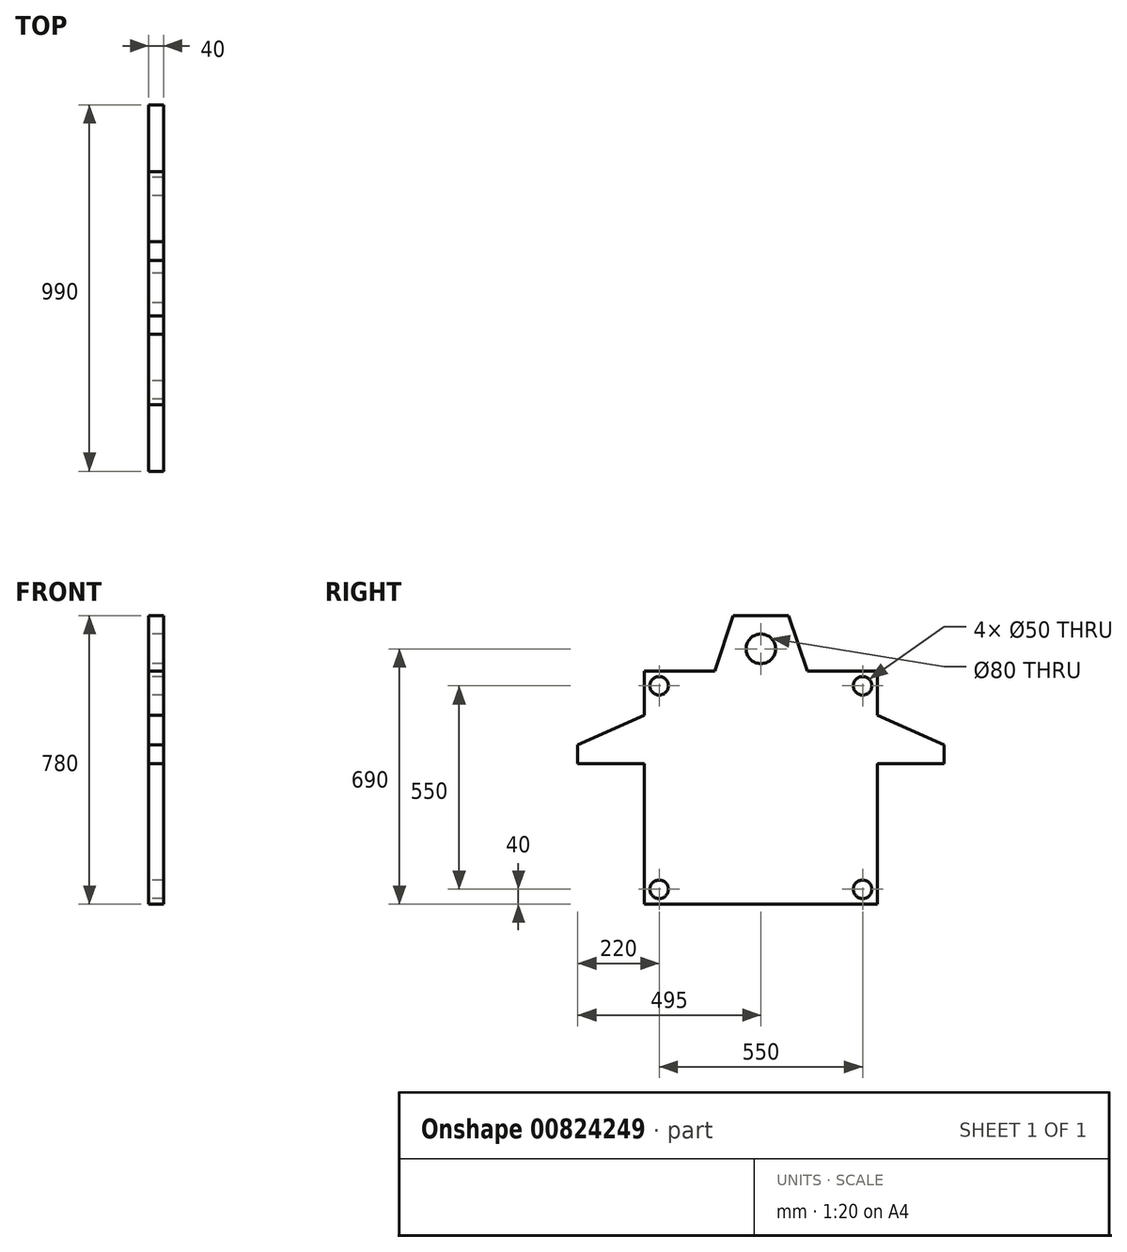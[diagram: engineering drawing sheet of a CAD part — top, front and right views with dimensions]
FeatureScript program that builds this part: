
annotation { "Feature Type Name" : "Feature", "Feature Type Description" : "" }
export const myFeature = defineFeature(function(context is Context, id is Id, definition is map)
    precondition{}
    {
        {
            var Q0;
            Q0=qCreatedBy(makeId("Right.planeOp"),FACE);
            var sketch = newSketch(context, id + "F0", { "sketchPlane" : qUnion([Q0])});
            skLineSegment(sketch, "E0.bottom", {"start": v(-315, 315) * mm, "end": v(-125, 315) * mm});
            skLineSegment(sketch, "E0.top", {"start": v(-315, -315) * mm, "end": v(-125, -315) * mm});
            skLineSegment(sketch, "E0.left", {"start": v(-315, 315) * mm, "end": v(-315, 195) * mm});
            skLineSegment(sketch, "E0.right", {"start": v(315, 315) * mm, "end": v(315, 195) * mm});
            skPoint(sketch, "E0.middle", {"position": v(0, 0) * mm});
            skLineSegment(sketch, "E1.top", {"start": v(75, 465) * mm, "end": v(-75, 465) * mm});
            skPoint(sketch, "E1.middle", {"position": v(0, 315) * mm});
            skLineSegment(sketch, "E2", {"start": v(-75, 465) * mm, "end": v(-125, 315) * mm});
            skLineSegment(sketch, "E3", {"start": v(75, 465) * mm, "end": v(125, 315) * mm});
            skPoint(sketch, "E4.MirrorP", {"position": v(0, -315) * mm});
            skLineSegment(sketch, "E5", {"start": v(-315, 195) * mm, "end": v(-495, 115) * mm});
            skLineSegment(sketch, "E6", {"start": v(-495, 115) * mm, "end": v(-495, 65) * mm});
            skLineSegment(sketch, "E7", {"start": v(-495, 65) * mm, "end": v(-315, 65) * mm});
            skLineSegment(sketch, "E8.MirrorCS", {"start": v(315, 195) * mm, "end": v(495, 115) * mm});
            skLineSegment(sketch, "E9.MirrorCS", {"start": v(495, 65) * mm, "end": v(315, 65) * mm});
            skLineSegment(sketch, "E10.MirrorCS", {"start": v(495, 115) * mm, "end": v(495, 65) * mm});
            skLineSegment(sketch, "E11.trimOffspring", {"start": v(125, -315) * mm, "end": v(315, -315) * mm});
            skLineSegment(sketch, "E12.trimOffspring", {"start": v(-315, 65) * mm, "end": v(-315, -315) * mm});
            skLineSegment(sketch, "E13.trimOffspring", {"start": v(315, 65) * mm, "end": v(315, -315) * mm});
            skLineSegment(sketch, "E14.trimOffspring", {"start": v(125, 315) * mm, "end": v(315, 315) * mm});
            skPoint(sketch, "E1.bottom.end.orphan", {"position": v(-75, 165) * mm});
            skPoint(sketch, "E1.bottom.start.orphan", {"position": v(75, 165) * mm});
            skCircle(sketch, "E15", {"center": v(-275, 275) * mm, "radius": 25 * mm});
            skCircle(sketch, "E16.0.1.0", {"center": v(-275, -275) * mm, "radius": 25 * mm});
            skCircle(sketch, "E16.1.0.0", {"center": v(275, 275) * mm, "radius": 25 * mm});
            skCircle(sketch, "E16.1.1.0", {"center": v(275, -275) * mm, "radius": 25 * mm});
            skLineSegment(sketch, "E16.direction1", {"start": v(-275, 275) * mm, "end": v(275, 275) * mm, "construction": true});
            skLineSegment(sketch, "E16.direction2", {"start": v(-275, 275) * mm, "end": v(-275, -275) * mm, "construction": true});
            skCircle(sketch, "E17", {"center": v(0, 375) * mm, "radius": 40 * mm});
            skLineSegment(sketch, "E18", {"start": v(-125, -315) * mm, "end": v(125, -315) * mm});
            skPoint(sketch, "E19.MirrorCS.start.orphan", {"position": v(75, -465) * mm});
            skPoint(sketch, "E20.MirrorCS.start.orphan", {"position": v(-75, -465) * mm});
            skSolve(sketch);
        }
        {
            var Q0;
            Q0=makeQuery(id+"F0.imprint","IMPRINT",FACE,{"disambiguationData":[TD([[makeQuery(id+"F0.imprint","IMPRINT",EDGE,{"derivedFrom":sQuery(id+"F0.wireOp",EDGE,"E0.bottom")}),-1.0]])]});
            extrude(context, id + "F1", {"entities" : qUnion([Q0]), "depth" : 40 * mm, "offsetDistance" : 25 * mm});
        }
    });
